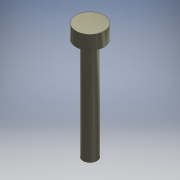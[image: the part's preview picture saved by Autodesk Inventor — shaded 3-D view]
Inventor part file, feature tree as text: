
AUTODESK INVENTOR PART (.ipt)
format: ipt  version: 2016 (Build 200138000, 138)  size: 94,720 bytes
history: native  units: mm
features: extrude x2, other x1, sketch x1
ambient origin geometry x8: Origin, YZ Plane, XZ Plane, XY Plane, X Axis, Y Axis, Z Axis, Center Point
bodies: Body1 (feature_tree)
feature tree (4):
  other  "ソリッド1"
  sketch  "スケッチ1"
  extrude  "押し出し1"  Depth=6.0mm
  extrude  "押し出し2"  Depth=3.0mm
